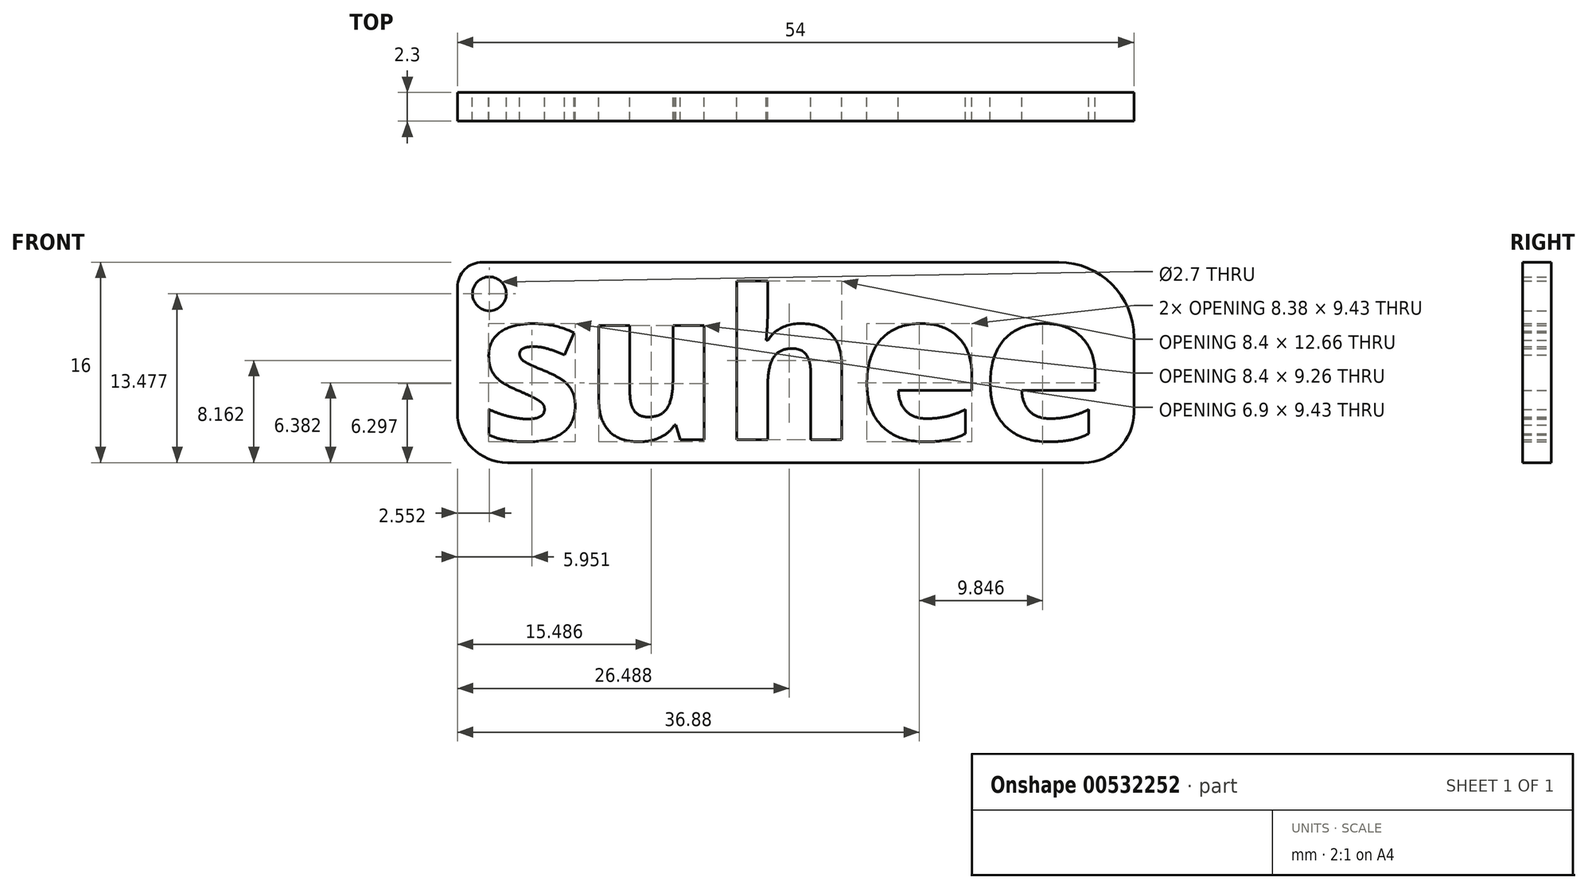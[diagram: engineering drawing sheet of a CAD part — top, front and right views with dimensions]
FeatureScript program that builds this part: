
annotation { "Feature Type Name" : "Feature", "Feature Type Description" : "" }
export const myFeature = defineFeature(function(context is Context, id is Id, definition is map)
    precondition{}
    {
        {
            var Q0;
            Q0=qCreatedBy(makeId("Front.planeOp"),FACE);
            var sketch = newSketch(context, id + "F0", { "sketchPlane" : qUnion([Q0])});
            skText(sketch, "E0", { "text": "suhee", "fontName": "OpenSans-Bold.ttf"});
            skLineSegment(sketch, "E1.bottom", {"start": v(23, -8) * mm, "end": v(-23, -8) * mm});
            skLineSegment(sketch, "E1.top", {"start": v(21, 8) * mm, "end": v(-25, 8) * mm});
            skLineSegment(sketch, "E1.left", {"start": v(27, -4) * mm, "end": v(27, 2) * mm});
            skLineSegment(sketch, "E1.right", {"start": v(-27, -4) * mm, "end": v(-27, 6) * mm});
            skPoint(sketch, "E1.middle", {"position": v(0, 0) * mm});
            skPoint(sketch, "E2.visualSharp", {"position": v(27, 8) * mm});
            skArc(sketch, "E2.filletArc", {"start": v(27, 2) * mm, "mid": v(25.24, 6.24) * mm, "end": v(21, 8) * mm});
            skPoint(sketch, "E3.visualSharp", {"position": v(27, -8) * mm});
            skArc(sketch, "E3.filletArc", {"start": v(23, -8) * mm, "mid": v(25.83, -6.83) * mm, "end": v(27, -4) * mm});
            skPoint(sketch, "E4.visualSharp", {"position": v(-27, -8) * mm});
            skArc(sketch, "E4.filletArc", {"start": v(-27, -4) * mm, "mid": v(-25.83, -6.83) * mm, "end": v(-23, -8) * mm});
            skPoint(sketch, "E5.visualSharp", {"position": v(-27, 8) * mm});
            skArc(sketch, "E5.filletArc", {"start": v(-25, 8) * mm, "mid": v(-26.41, 7.41) * mm, "end": v(-27, 6) * mm});
            skCircle(sketch, "E6", {"center": v(-24.45, 5.48) * mm, "radius": 1.35 * mm});
            const initialGuessF0  = {"E0": [-0.02525, -0.00617, 1, 0, 0.012]};
            skSetInitialGuess(sketch, initialGuessF0);
            skSolve(sketch);
        }
        {
            var Q0;
            Q0=makeQuery(id+"F0.imprint","IMPRINT",FACE,{"disambiguationData":[TD([[makeQuery(id+"F0.imprint","IMPRINT",EDGE,{"derivedFrom":sQuery(id+"F0.wireOp",EDGE,"E0.sketch_text.stroke-0")}),1.0]])]});
            extrude(context, id + "F1", {"entities" : qUnion([Q0]), "depth" : 2.3 * mm, "offsetDistance" : 25 * mm});
        }
    });
